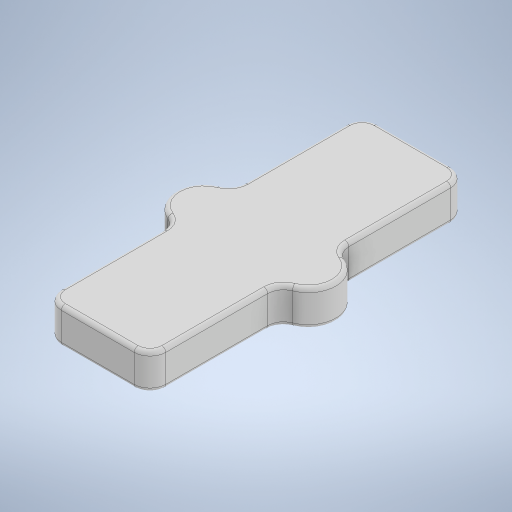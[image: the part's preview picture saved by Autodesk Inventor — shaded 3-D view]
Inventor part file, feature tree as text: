
AUTODESK INVENTOR PART (.ipt)
format: ipt  version: 2023 (Build 270158000, 158)  size: 310,272 bytes
history: native  units: mm
features: extrude x3, sketch x2, fillet x2, chamfer x1
ambient origin geometry x8: Origin, YZ Plane, XZ Plane, XY Plane, X Axis, Y Axis, Z Axis, Center Point
bodies: Solid1 (feature_tree)
feature tree (8):
  extrude  "Extrusion1"  Depth=40.0mm
  sketch  "Sketch2"  dims[d2=4.5mm d3=0.0mm d4=4.1mm d5=7.0mm d6=4.5mm d7=0.0mm d8=3.0mm d9=0.0mm d10=2.0mm d11=0.5mm d12=0.25mm d13=2.0mm d14=45.0deg]
  extrude  "Extrusion2"  Depth=2.0mm
  extrude  "Extrusion3"  Depth=2.0mm
  fillet  "Fillet1"  Radius=4.5mm
  fillet  "Fillet2"  Radius=3.0mm
  chamfer  "Chamfer1"  Distance=2.0mm
  sketch  "Sketch1"  dims[d0=13.2mm d1=40.0mm]
